# Revit family: QMXU
name_source: partatom
category: Mechanical Equipment
units: mm (PartAtom-declared; Revit-internal decimal feet)

## family parameters
Always vertical = Yes
Cut with Voids When Loaded = No
Part Type = Normal
Room Calculation Point = No
Round Connector Dimension = Use Diameter
Shared = No
Work Plane-Based = No

## types (35) — shared parameters
0 = 0' - 0"
1" = 0' - 1"
1.5 = 0' - 1 1/2"
2" = 0' - 2"
2' = 2' - 0"
3" = 0' - 3"
4" = 0' - 4"
Manufacturer = Loren Cook Company
ONE EIGTH = 0' - 0 1/8"
URL = www.lorencook.com

## per-type parameters (varying)
- 90_QMXU: (B/2)-.125"=0' - 9 7/8"; (FAN_RADIUS)*.75=0' - 4 13/16"; A=3' - 4 9/16"; A/2=1' - 8 9/32"; B=1' - 8"; B/2=0' - 10"; C=0' - 3"; C/2=0' - 1 1/2"; D=3' - 1 3/8"; D-(G/2)=2' - 5 7/8"; DC/2=0' - 6 13/32"; DUCT_COLLAR=1' - 0 13/16"; E=1' - 10 1/2"; F=1' - 9 1/4"; FAN_DIA=1' - 0 13/16"; FAN_RAD+1.5"=0' - 7 29/32"; FAN_RADIUS=0' - 6 13/32"; FAN_RADIUS/5=0' - 1 9/32"; G=1' - 3"; G/2=0' - 7 1/2"; MC_LENGTH=-1' - 3 29/32"; Model=QMXU; QMX_LENGTH=1' - 7 7/8"; T_SQ=1' - 3 1/2"; T_SQ/2=0' - 7 3/4"; Type Comments=Mixed-Flow Upblast Blower Low Pressure Belt Drive Arrangement 9
- 300_QMXU: (B/2)-.125"=2' - 2 7/8"; (FAN_RADIUS)*.75=1' - 3 15/16"; A=7' - 6 1/4"; A/2=3' - 9 1/8"; B=4' - 6"; B/2=2' - 3"; C=0' - 3"; C/2=0' - 1 1/2"; D=6' - 10"; D-(G/2)=5' - 6 3/4"; DC/2=1' - 9 1/4"; DUCT_COLLAR=3' - 6 1/2"; E=3' - 4"; F=3' - 1 5/8"; FAN_DIA=3' - 6 1/2"; FAN_RAD+1.5"=1' - 10 3/4"; FAN_RADIUS=1' - 9 1/4"; FAN_RADIUS/5=0' - 4 1/4"; G=2' - 6 1/2"; G/2=1' - 3 1/4"; MC_LENGTH=-3' - 7 3/16"; Model=QMXU; QMX_LENGTH=4' - 6"; T_SQ=4' - 1 1/2"; T_SQ/2=2' - 0 3/4"; Type Comments=Mixed-Flow Upblast Blower Low Pressure Belt Drive Arrangement 9
- 120_QMXU: (B/2)-.125"=0' - 11 7/8"; (FAN_RADIUS)*.75=0' - 6 13/32"; A=3' - 9 11/16"; A/2=1' - 10 27/32"; B=2' - 0"; B/2=1' - 0"; C=0' - 3"; C/2=0' - 1 1/2"; D=3' - 7 5/8"; D-(G/2)=2' - 11 1/8"; DC/2=0' - 8 17/32"; DUCT_COLLAR=1' - 5 1/16"; E=2' - 1 3/8"; F=2' - 0 3/8"; FAN_DIA=1' - 5 1/16"; FAN_RAD+1.5"=0' - 10 1/32"; FAN_RADIUS=0' - 8 17/32"; FAN_RADIUS/5=0' - 1 23/32"; G=1' - 5"; G/2=0' - 8 1/2"; MC_LENGTH=-1' - 7 3/16"; Model=QMXU; QMX_LENGTH=2' - 0"; T_SQ=1' - 7 1/2"; T_SQ/2=0' - 9 3/4"; Type Comments=Mixed-Flow Upblast Blower Low Pressure Belt Drive Arrangement 9
- 135_QMXU: (B/2)-.125"=1' - 0 7/8"; (FAN_RADIUS)*.75=0' - 7 7/32"; A=4' - 1 11/16"; A/2=2' - 0 27/32"; B=2' - 2"; B/2=1' - 1"; C=0' - 3"; C/2=0' - 1 1/2"; D=3' - 10 1/2"; D-(G/2)=3' - 1 1/2"; DC/2=0' - 9 5/8"; DUCT_COLLAR=1' - 7 1/4"; E=2' - 3 1/4"; F=2' - 1 3/8"; FAN_DIA=1' - 7 1/4"; FAN_RAD+1.5"=0' - 11 1/8"; FAN_RADIUS=0' - 9 5/8"; FAN_RADIUS/5=0' - 1 15/16"; G=1' - 6"; G/2=0' - 9"; MC_LENGTH=-1' - 9 19/32"; Model=QMXU; QMX_LENGTH=2' - 3"; T_SQ=1' - 9 1/2"; T_SQ/2=0' - 10 3/4"; Type Comments=Mixed-Flow Upblast Blower Low Pressure Belt Drive Arrangement 9
- 165_QMXU: (B/2)-.125"=1' - 5 3/8"; (FAN_RADIUS)*.75=0' - 8 13/16"; A=4' - 10 11/16"; A/2=2' - 5 11/32"; B=2' - 11"; B/2=1' - 5 1/2"; C=0' - 3"; C/2=0' - 1 1/2"; D=4' - 7"; D-(G/2)=3' - 8 1/2"; DC/2=0' - 11 3/4"; DUCT_COLLAR=1' - 11 1/2"; E=2' - 5 13/16"; F=2' - 3 1/8"; FAN_DIA=1' - 11 1/2"; FAN_RAD+1.5"=1' - 1 1/4"; FAN_RADIUS=0' - 11 3/4"; FAN_RADIUS/5=0' - 2 11/32"; G=1' - 9"; G/2=0' - 10 1/2"; MC_LENGTH=-2' - 2 13/32"; Model=QMXU; QMX_LENGTH=2' - 9"; T_SQ=2' - 6 1/2"; T_SQ/2=1' - 3 1/4"; Type Comments=Mixed-Flow Upblast Blower Low Pressure Belt Drive Arrangement 9
- 180_QMXU: (B/2)-.125"=1' - 6 3/8"; (FAN_RADIUS)*.75=0' - 9 5/8"; A=5' - 1 11/16"; A/2=2' - 6 27/32"; B=3' - 1"; B/2=1' - 6 1/2"; C=0' - 3"; C/2=0' - 1 1/2"; D=4' - 9 3/4"; D-(G/2)=3' - 10 3/4"; DC/2=1' - 0 13/16"; DUCT_COLLAR=2' - 1 5/8"; E=2' - 6 3/4"; F=2' - 4 1/8"; FAN_DIA=2' - 1 5/8"; FAN_RAD+1.5"=1' - 2 5/16"; FAN_RADIUS=1' - 0 13/16"; FAN_RADIUS/5=0' - 2 9/16"; G=1' - 10"; G/2=0' - 11"; MC_LENGTH=-2' - 4"; Model=QMXU; QMX_LENGTH=2' - 11"; T_SQ=2' - 8 1/2"; T_SQ/2=1' - 4 1/4"; Type Comments=Mixed-Flow Upblast Blower Low Pressure Belt Drive Arrangement 9
- 202_QMXU: (B/2)-.125"=1' - 7 7/8"; (FAN_RADIUS)*.75=0' - 9 5/8"; A=5' - 5 11/16"; A/2=2' - 8 27/32"; B=3' - 4"; B/2=1' - 8"; C=0' - 3"; C/2=0' - 1 1/2"; D=5' - 1 13/16"; D-(G/2)=4' - 2 1/16"; DC/2=1' - 2 3/8"; DUCT_COLLAR=2' - 4 3/4"; E=2' - 8 1/8"; F=2' - 5 1/2"; FAN_DIA=2' - 1 5/8"; FAN_RAD+1.5"=1' - 2 5/16"; FAN_RADIUS=1' - 0 13/16"; FAN_RADIUS/5=0' - 2 9/16"; G=1' - 11 1/2"; G/2=0' - 11 3/4"; MC_LENGTH=-2' - 4"; Model=QMXU; QMX_LENGTH=2' - 11"; T_SQ=2' - 11 1/2"; T_SQ/2=1' - 5 3/4"; Type Comments=Mixed-Flow Upblast Blower Low Pressure Belt Drive Arrangement 9
- 225_QMXU: (B/2)-.125"=1' - 9 3/8"; (FAN_RADIUS)*.75=0' - 11 31/32"; A=5' - 10 11/16"; A/2=2' - 11 11/32"; B=3' - 7"; B/2=1' - 9 1/2"; C=0' - 3"; C/2=0' - 1 1/2"; D=5' - 8 1/8"; D-(G/2)=4' - 7 5/8"; DC/2=1' - 3 31/32"; DUCT_COLLAR=2' - 7 15/16"; E=2' - 11 1/2"; F=2' - 9"; FAN_DIA=2' - 7 15/16"; FAN_RAD+1.5"=1' - 5 15/32"; FAN_RADIUS=1' - 3 31/32"; FAN_RADIUS/5=0' - 3 3/16"; G=2' - 1"; G/2=1' - 0 1/2"; MC_LENGTH=-2' - 8 13/16"; Model=QMXU; QMX_LENGTH=3' - 5"; T_SQ=3' - 2 1/2"; T_SQ/2=1' - 7 1/4"; Type Comments=Mixed-Flow Upblast Blower Low Pressure Belt Drive Arrangement 9
- 245_QMXU: (B/2)-.125"=1' - 10 7/8"; (FAN_RADIUS)*.75=1' - 1 1/32"; A=6' - 4 5/8"; A/2=3' - 2 5/16"; B=3' - 10"; B/2=1' - 11"; C=0' - 3"; C/2=0' - 1 1/2"; D=5' - 11 13/16"; D-(G/2)=4' - 10 5/16"; DC/2=1' - 5 3/8"; DUCT_COLLAR=2' - 10 3/4"; E=3' - 0 5/8"; F=2' - 10 1/8"; FAN_DIA=2' - 10 3/4"; FAN_RAD+1.5"=1' - 6 7/8"; FAN_RADIUS=1' - 5 3/8"; FAN_RADIUS/5=0' - 3 15/32"; G=2' - 3"; G/2=1' - 1 1/2"; MC_LENGTH=-2' - 11 19/32"; Model=QMXU; QMX_LENGTH=3' - 8 1/2"; T_SQ=3' - 5 1/2"; T_SQ/2=1' - 8 3/4"; Type Comments=Mixed-Flow Upblast Blower Low Pressure Belt Drive Arrangement 9
- 270_QMXU: (B/2)-.125"=2' - 0 7/8"; (FAN_RADIUS)*.75=1' - 2 3/8"; A=6' - 8 7/8"; A/2=3' - 4 7/16"; B=4' - 2"; B/2=2' - 1"; C=0' - 3"; C/2=0' - 1 1/2"; D=6' - 4 5/16"; D-(G/2)=5' - 2 1/16"; DC/2=1' - 7 5/32"; DUCT_COLLAR=3' - 2 5/16"; E=3' - 2"; F=2' - 11 9/16"; FAN_DIA=3' - 2 5/16"; FAN_RAD+1.5"=1' - 8 21/32"; FAN_RADIUS=1' - 7 5/32"; FAN_RADIUS/5=0' - 3 27/32"; G=2' - 4 1/2"; G/2=1' - 2 1/4"; MC_LENGTH=-3' - 1 19/32"; Model=QMXU; QMX_LENGTH=3' - 11"; T_SQ=3' - 9 1/2"; T_SQ/2=1' - 10 3/4"; Type Comments=Mixed-Flow Upblast Blower Low Pressure Belt Drive Arrangement 9
- 120_QMXU-HP: (B/2)-.125"=0' - 11 7/8"; (FAN_RADIUS)*.75=0' - 6 13/32"; A=3' - 9 11/16"; A/2=1' - 10 27/32"; B=2' - 0"; B/2=1' - 0"; C=0' - 3"; C/2=0' - 1 1/2"; D=3' - 7 5/8"; D-(G/2)=2' - 11 1/8"; DC/2=0' - 8 17/32"; DUCT_COLLAR=1' - 5 1/16"; E=2' - 1 3/8"; F=2' - 0 3/8"; FAN_DIA=1' - 5 1/16"; FAN_RAD+1.5"=0' - 10 1/32"; FAN_RADIUS=0' - 8 17/32"; FAN_RADIUS/5=0' - 1 23/32"; G=1' - 5"; G/2=0' - 8 1/2"; MC_LENGTH=-1' - 7 3/16"; Model=QMXU-HP; QMX_LENGTH=2' - 0"; T_SQ=1' - 7 1/2"; T_SQ/2=0' - 9 3/4"; Type Comments=Mixed-Flow Upblast Blower High Pressure Belt Drive Arrangement 9
- 135_QMXU-HP: (B/2)-.125"=1' - 0 7/8"; (FAN_RADIUS)*.75=0' - 7 7/32"; A=4' - 1 11/16"; A/2=2' - 0 27/32"; B=2' - 2"; B/2=1' - 1"; C=0' - 3"; C/2=0' - 1 1/2"; D=3' - 10 1/2"; D-(G/2)=3' - 1 1/2"; DC/2=0' - 9 5/8"; DUCT_COLLAR=1' - 7 1/4"; E=2' - 3 1/4"; F=2' - 1 3/8"; FAN_DIA=1' - 7 1/4"; FAN_RAD+1.5"=0' - 11 1/8"; FAN_RADIUS=0' - 9 5/8"; FAN_RADIUS/5=0' - 1 15/16"; G=1' - 6"; G/2=0' - 9"; MC_LENGTH=-1' - 9 19/32"; Model=QMXU-HP; QMX_LENGTH=2' - 3"; T_SQ=1' - 9 1/2"; T_SQ/2=0' - 10 3/4"; Type Comments=Mixed-Flow Upblast Blower High Pressure Belt Drive Arrangement 9
- 150_QMXU-HP: (B/2)-.125"=1' - 2 7/8"; (FAN_RADIUS)*.75=0' - 8 1/32"; A=4' - 6 11/16"; A/2=2' - 3 11/32"; B=2' - 6"; B/2=1' - 3"; C=0' - 3"; C/2=0' - 1 1/2"; D=4' - 3"; D-(G/2)=3' - 5"; DC/2=0' - 10 11/16"; DUCT_COLLAR=1' - 9 3/8"; E=2' - 4"; F=2' - 2 1/8"; FAN_DIA=1' - 9 3/8"; FAN_RAD+1.5"=1' - 0 3/16"; FAN_RADIUS=0' - 10 11/16"; FAN_RADIUS/5=0' - 2 1/8"; G=1' - 8"; G/2=0' - 10"; MC_LENGTH=-2' - 0"; Model=QMXU-HP; QMX_LENGTH=2' - 6"; T_SQ=2' - 1 1/2"; T_SQ/2=1' - 0 3/4"; Type Comments=Mixed-Flow Upblast Blower High Pressure Belt Drive Arrangement 9
- 165_QMXU-HP: (B/2)-.125"=1' - 5 3/8"; (FAN_RADIUS)*.75=0' - 8 13/16"; A=4' - 10 11/16"; A/2=2' - 5 11/32"; B=2' - 11"; B/2=1' - 5 1/2"; C=0' - 3"; C/2=0' - 1 1/2"; D=4' - 7"; D-(G/2)=3' - 8 1/2"; DC/2=0' - 11 3/4"; DUCT_COLLAR=1' - 11 1/2"; E=2' - 5 13/16"; F=2' - 3 1/8"; FAN_DIA=1' - 11 1/2"; FAN_RAD+1.5"=1' - 1 1/4"; FAN_RADIUS=0' - 11 3/4"; FAN_RADIUS/5=0' - 2 11/32"; G=1' - 9"; G/2=0' - 10 1/2"; MC_LENGTH=-2' - 2 13/32"; Model=QMXU-HP; QMX_LENGTH=2' - 9"; T_SQ=2' - 6 1/2"; T_SQ/2=1' - 3 1/4"; Type Comments=Mixed-Flow Upblast Blower High Pressure Belt Drive Arrangement 9
- 180_QMXU-HP: (B/2)-.125"=1' - 6 3/8"; (FAN_RADIUS)*.75=0' - 9 5/8"; A=5' - 1 11/16"; A/2=2' - 6 27/32"; B=3' - 1"; B/2=1' - 6 1/2"; C=0' - 3"; C/2=0' - 1 1/2"; D=4' - 9 3/4"; D-(G/2)=3' - 10 3/4"; DC/2=1' - 0 13/16"; DUCT_COLLAR=2' - 1 5/8"; E=2' - 6 3/4"; F=2' - 4 1/8"; FAN_DIA=2' - 1 5/8"; FAN_RAD+1.5"=1' - 2 5/16"; FAN_RADIUS=1' - 0 13/16"; FAN_RADIUS/5=0' - 2 9/16"; G=1' - 10"; G/2=0' - 11"; MC_LENGTH=-2' - 4"; Model=QMXU-HP; QMX_LENGTH=2' - 11"; T_SQ=2' - 8 1/2"; T_SQ/2=1' - 4 1/4"; Type Comments=Mixed-Flow Upblast Blower High Pressure Belt Drive Arrangement 9
- 202_QMXU-HP: (B/2)-.125"=1' - 7 7/8"; (FAN_RADIUS)*.75=0' - 9 5/8"; A=5' - 5 11/16"; A/2=2' - 8 27/32"; B=3' - 4"; B/2=1' - 8"; C=0' - 3"; C/2=0' - 1 1/2"; D=5' - 1 13/16"; D-(G/2)=4' - 2 1/16"; DC/2=1' - 2 3/8"; DUCT_COLLAR=2' - 4 3/4"; E=2' - 8 1/8"; F=2' - 5 1/2"; FAN_DIA=2' - 1 5/8"; FAN_RAD+1.5"=1' - 2 5/16"; FAN_RADIUS=1' - 0 13/16"; FAN_RADIUS/5=0' - 2 9/16"; G=1' - 11 1/2"; G/2=0' - 11 3/4"; MC_LENGTH=-2' - 4"; Model=QMXU-HP; QMX_LENGTH=2' - 11"; T_SQ=2' - 11 1/2"; T_SQ/2=1' - 5 3/4"; Type Comments=Mixed-Flow Upblast Blower High Pressure Belt Drive Arrangement 9
- 225_QMXU-HP: (B/2)-.125"=1' - 9 3/8"; (FAN_RADIUS)*.75=0' - 11 31/32"; A=5' - 10 11/16"; A/2=2' - 11 11/32"; B=3' - 7"; B/2=1' - 9 1/2"; C=0' - 3"; C/2=0' - 1 1/2"; D=5' - 8 1/8"; D-(G/2)=4' - 7 5/8"; DC/2=1' - 3 31/32"; DUCT_COLLAR=2' - 7 15/16"; E=2' - 11 1/2"; F=2' - 9"; FAN_DIA=2' - 7 15/16"; FAN_RAD+1.5"=1' - 5 15/32"; FAN_RADIUS=1' - 3 31/32"; FAN_RADIUS/5=0' - 3 3/16"; G=2' - 1"; G/2=1' - 0 1/2"; MC_LENGTH=-2' - 8 13/16"; Model=QMXU-HP; QMX_LENGTH=3' - 5"; T_SQ=3' - 2 1/2"; T_SQ/2=1' - 7 1/4"; Type Comments=Mixed-Flow Upblast Blower High Pressure Belt Drive Arrangement 9
- 245_QMXU-HP: (B/2)-.125"=1' - 10 7/8"; (FAN_RADIUS)*.75=1' - 1 1/32"; A=6' - 4 5/8"; A/2=3' - 2 5/16"; B=3' - 10"; B/2=1' - 11"; C=0' - 3"; C/2=0' - 1 1/2"; D=5' - 11 13/16"; D-(G/2)=4' - 10 5/16"; DC/2=1' - 5 3/8"; DUCT_COLLAR=2' - 10 3/4"; E=3' - 0 5/8"; F=2' - 10 1/8"; FAN_DIA=2' - 10 3/4"; FAN_RAD+1.5"=1' - 6 7/8"; FAN_RADIUS=1' - 5 3/8"; FAN_RADIUS/5=0' - 3 15/32"; G=2' - 3"; G/2=1' - 1 1/2"; MC_LENGTH=-2' - 11 19/32"; Model=QMXU-HP; QMX_LENGTH=3' - 8 1/2"; T_SQ=3' - 5 1/2"; T_SQ/2=1' - 8 3/4"; Type Comments=Mixed-Flow Upblast Blower High Pressure Belt Drive Arrangement 9
- 270_QMXU-HP: (B/2)-.125"=2' - 0 7/8"; (FAN_RADIUS)*.75=1' - 2 3/8"; A=6' - 8 7/8"; A/2=3' - 4 7/16"; B=4' - 2"; B/2=2' - 1"; C=0' - 3"; C/2=0' - 1 1/2"; D=6' - 4 5/16"; D-(G/2)=5' - 2 1/16"; DC/2=1' - 7 5/32"; DUCT_COLLAR=3' - 2 5/16"; E=3' - 2"; F=2' - 11 9/16"; FAN_DIA=3' - 2 5/16"; FAN_RAD+1.5"=1' - 8 21/32"; FAN_RADIUS=1' - 7 5/32"; FAN_RADIUS/5=0' - 3 27/32"; G=2' - 4 1/2"; G/2=1' - 2 1/4"; MC_LENGTH=-3' - 1 19/32"; Model=QMXU-HP; QMX_LENGTH=3' - 11"; T_SQ=3' - 9 1/2"; T_SQ/2=1' - 10 3/4"; Type Comments=Mixed-Flow Upblast Blower High Pressure Belt Drive Arrangement 9
- 300_QMXU-HP: (B/2)-.125"=2' - 2 7/8"; (FAN_RADIUS)*.75=1' - 3 15/16"; A=7' - 6 1/4"; A/2=3' - 9 1/8"; B=4' - 6"; B/2=2' - 3"; C=0' - 3"; C/2=0' - 1 1/2"; D=6' - 10"; D-(G/2)=5' - 6 3/4"; DC/2=1' - 9 1/4"; DUCT_COLLAR=3' - 6 1/2"; E=3' - 4"; F=3' - 1 5/8"; FAN_DIA=3' - 6 1/2"; FAN_RAD+1.5"=1' - 10 3/4"; FAN_RADIUS=1' - 9 1/4"; FAN_RADIUS/5=0' - 4 1/4"; G=2' - 6 1/2"; G/2=1' - 3 1/4"; MC_LENGTH=-3' - 7 3/16"; Model=QMXU-HP; QMX_LENGTH=4' - 6"; T_SQ=4' - 1 1/2"; T_SQ/2=2' - 0 3/4"; Type Comments=Mixed-Flow Upblast Blower High Pressure Belt Drive Arrangement 9
- 90_QMXU-HP: (B/2)-.125"=0' - 9 7/8"; (FAN_RADIUS)*.75=0' - 4 13/16"; A=3' - 4 9/16"; A/2=1' - 8 9/32"; B=1' - 8"; B/2=0' - 10"; C=0' - 3"; C/2=0' - 1 1/2"; D=3' - 1 3/8"; D-(G/2)=2' - 5 7/8"; DC/2=0' - 6 13/32"; DUCT_COLLAR=1' - 0 13/16"; E=1' - 10 1/2"; F=1' - 9 1/4"; FAN_DIA=1' - 0 13/16"; FAN_RAD+1.5"=0' - 7 29/32"; FAN_RADIUS=0' - 6 13/32"; FAN_RADIUS/5=0' - 1 9/32"; G=1' - 3"; G/2=0' - 7 1/2"; MC_LENGTH=-1' - 3 29/32"; Model=QMXU-HP; QMX_LENGTH=1' - 7 7/8"; T_SQ=1' - 3 1/2"; T_SQ/2=0' - 7 3/4"; Type Comments=Mixed-Flow Upblast Blower High Pressure Belt Drive Arrangement 9
- 330_QMXU: (B/2)-.125"=2' - 4 7/8"; (FAN_RADIUS)*.75=1' - 5 17/32"; A=7' - 2 3/4"; A/2=3' - 7 3/8"; B=4' - 10"; B/2=2' - 5"; C=0' - 3"; C/2=0' - 1 1/2"; D=7' - 5 1/4"; D-(G/2)=6' - 1"; DC/2=1' - 11 3/8"; DUCT_COLLAR=3' - 10 3/4"; E=3' - 8 5/8"; F=3' - 5 11/16"; FAN_DIA=3' - 10 3/4"; FAN_RAD+1.5"=2' - 0 7/8"; FAN_RADIUS=1' - 11 3/8"; FAN_RADIUS/5=0' - 4 11/16"; G=2' - 8 1/2"; G/2=1' - 4 1/4"; MC_LENGTH=-3' - 1 13/32"; Model=QMXU; QMX_LENGTH=3' - 10 3/4"; T_SQ=4' - 5 1/2"; T_SQ/2=2' - 2 3/4"; Type Comments=Mixed-Flow Upblast Blower Low Pressure Belt Drive Arrangement 9
- 365_QMXU: (B/2)-.125"=2' - 7 7/8"; (FAN_RADIUS)*.75=1' - 7 13/32"; A=8' - 8 7/8"; A/2=4' - 4 7/16"; B=5' - 4"; B/2=2' - 8"; C=0' - 3"; C/2=0' - 1 1/2"; D=8' - 0 1/4"; D-(G/2)=6' - 6 3/4"; DC/2=2' - 1 7/8"; DUCT_COLLAR=4' - 3 3/4"; E=3' - 10 5/8"; F=3' - 7 5/8"; FAN_DIA=4' - 3 3/4"; FAN_RAD+1.5"=2' - 3 3/8"; FAN_RADIUS=2' - 1 7/8"; FAN_RADIUS/5=0' - 5 3/16"; G=2' - 11"; G/2=1' - 5 1/2"; MC_LENGTH=-4' - 3 3/16"; Model=QMXU; QMX_LENGTH=5' - 4"; T_SQ=4' - 11 1/2"; T_SQ/2=2' - 5 3/4"; Type Comments=Mixed-Flow Upblast Blower Low Pressure Belt Drive Arrangement 9
- 402_QMXU: (B/2)-.125"=2' - 10 3/8"; (FAN_RADIUS)*.75=1' - 9 11/32"; A=9' - 4 3/8"; A/2=4' - 8 3/16"; B=5' - 9"; B/2=2' - 10 1/2"; C=0' - 3"; C/2=0' - 1 1/2"; D=8' - 9"; D-(G/2)=7' - 2"; DC/2=2' - 4 15/32"; DUCT_COLLAR=4' - 8 15/16"; E=4' - 4"; F=4' - 0 3/8"; FAN_DIA=4' - 8 15/16"; FAN_RAD+1.5"=2' - 5 31/32"; FAN_RADIUS=2' - 4 15/32"; FAN_RADIUS/5=0' - 5 11/16"; G=3' - 2"; G/2=1' - 7"; MC_LENGTH=-4' - 6 13/16"; Model=QMXU; QMX_LENGTH=5' - 8 1/2"; T_SQ=5' - 4 1/2"; T_SQ/2=2' - 8 1/4"; Type Comments=Mixed-Flow Upblast Blower Low Pressure Belt Drive Arrangement 9
- 445_QMXU: (B/2)-.125"=3' - 1 3/8"; (FAN_RADIUS)*.75=1' - 11 21/32"; A=10' - 0 7/8"; A/2=5' - 0 7/16"; B=6' - 3"; B/2=3' - 1 1/2"; C=0' - 3"; C/2=0' - 1 1/2"; D=9' - 4 7/16"; D-(G/2)=7' - 7 15/16"; DC/2=2' - 7 17/32"; DUCT_COLLAR=5' - 3 1/16"; E=4' - 6 3/8"; F=4' - 2 11/16"; FAN_DIA=5' - 3 1/16"; FAN_RAD+1.5"=2' - 9 1/32"; FAN_RADIUS=2' - 7 17/32"; FAN_RADIUS/5=0' - 6 5/16"; G=3' - 5"; G/2=1' - 8 1/2"; MC_LENGTH=-4' - 11 3/16"; Model=QMXU; QMX_LENGTH=6' - 2"; T_SQ=5' - 10 1/2"; T_SQ/2=2' - 11 1/4"; Type Comments=Mixed-Flow Upblast Blower Low Pressure Belt Drive Arrangement 9
- 490_QMXU: (B/2)-.125"=3' - 4 7/8"; (FAN_RADIUS)*.75=2' - 2 1/32"; A=10' - 11 3/8"; A/2=5' - 5 11/16"; B=6' - 10"; B/2=3' - 5"; C=0' - 4"; C/2=0' - 2"; D=10' - 2 1/2"; D-(G/2)=8' - 4 1/2"; DC/2=2' - 10 11/16"; DUCT_COLLAR=5' - 9 3/8"; E=4' - 11 5/8"; F=4' - 7 1/16"; FAN_DIA=5' - 9 3/8"; FAN_RAD+1.5"=3' - 0 3/16"; FAN_RADIUS=2' - 10 11/16"; FAN_RADIUS/5=0' - 6 15/16"; G=3' - 8"; G/2=1' - 10"; MC_LENGTH=-5' - 4 13/32"; Model=QMXU; QMX_LENGTH=6' - 8 1/2"; T_SQ=6' - 5 1/2"; T_SQ/2=3' - 2 3/4"; Type Comments=Mixed-Flow Upblast Blower Low Pressure Belt Drive Arrangement 9
- 540_QMXU: (B/2)-.125"=3' - 8 7/8"; (FAN_RADIUS)*.75=2' - 4 21/32"; A=11' - 9 7/8"; A/2=5' - 10 15/16"; B=7' - 6"; B/2=3' - 9"; C=0' - 4"; C/2=0' - 2"; D=10' - 11 7/8"; D-(G/2)=8' - 11 7/8"; DC/2=3' - 2 7/32"; DUCT_COLLAR=6' - 4 7/16"; E=5' - 2 1/4"; F=4' - 9 3/4"; FAN_DIA=6' - 4 7/16"; FAN_RAD+1.5"=3' - 3 23/32"; FAN_RADIUS=3' - 2 7/32"; FAN_RADIUS/5=0' - 7 21/32"; G=4' - 0"; G/2=2' - 0"; MC_LENGTH=-5' - 9 19/32"; Model=QMXU; QMX_LENGTH=7' - 3"; T_SQ=7' - 1 1/2"; T_SQ/2=3' - 6 3/4"; Type Comments=Mixed-Flow Upblast Blower Low Pressure Belt Drive Arrangement 9
- 600_QMXU: (B/2)-.125"=4' - 0 7/8"; (FAN_RADIUS)*.75=2' - 7 27/32"; A=12' - 10 3/8"; A/2=6' - 5 3/16"; B=8' - 2"; B/2=4' - 1"; C=0' - 4"; C/2=0' - 2"; D=11' - 10"; D-(G/2)=9' - 8"; DC/2=3' - 6 7/16"; DUCT_COLLAR=7' - 0 7/8"; E=5' - 5 1/2"; F=5' - 1"; FAN_DIA=7' - 0 7/8"; FAN_RAD+1.5"=3' - 7 15/16"; FAN_RADIUS=3' - 6 7/16"; FAN_RADIUS/5=0' - 8 1/2"; G=4' - 4"; G/2=2' - 2"; MC_LENGTH=-6' - 4 13/32"; Model=QMXU; QMX_LENGTH=7' - 11 1/2"; T_SQ=7' - 9 1/2"; T_SQ/2=3' - 10 3/4"; Type Comments=Mixed-Flow Upblast Blower  Low Pressure Belt Drive Arrangement 9
- 330_QMXU-HP: (B/2)-.125"=2' - 4 7/8"; (FAN_RADIUS)*.75=1' - 5 17/32"; A=7' - 2 3/4"; A/2=3' - 7 3/8"; B=4' - 10"; B/2=2' - 5"; C=0' - 3"; C/2=0' - 1 1/2"; D=7' - 5 1/4"; D-(G/2)=6' - 1"; DC/2=1' - 11 3/8"; DUCT_COLLAR=3' - 10 3/4"; E=3' - 8 5/8"; F=3' - 5 11/16"; FAN_DIA=3' - 10 3/4"; FAN_RAD+1.5"=2' - 0 7/8"; FAN_RADIUS=1' - 11 3/8"; FAN_RADIUS/5=0' - 4 11/16"; G=2' - 8 1/2"; G/2=1' - 4 1/4"; MC_LENGTH=-3' - 1 13/32"; Model=QMXU-HP; QMX_LENGTH=3' - 10 3/4"; T_SQ=4' - 5 1/2"; T_SQ/2=2' - 2 3/4"; Type Comments=Mixed-Flow Upblast Blower High Pressure Belt Drive Arrangement 9
- 365_QMXU-HP: (B/2)-.125"=2' - 7 7/8"; (FAN_RADIUS)*.75=1' - 7 13/32"; A=8' - 8 7/8"; A/2=4' - 4 7/16"; B=5' - 4"; B/2=2' - 8"; C=0' - 3"; C/2=0' - 1 1/2"; D=8' - 0 1/4"; D-(G/2)=6' - 6 3/4"; DC/2=2' - 1 7/8"; DUCT_COLLAR=4' - 3 3/4"; E=3' - 10 5/8"; F=3' - 7 5/8"; FAN_DIA=4' - 3 3/4"; FAN_RAD+1.5"=2' - 3 3/8"; FAN_RADIUS=2' - 1 7/8"; FAN_RADIUS/5=0' - 5 3/16"; G=2' - 11"; G/2=1' - 5 1/2"; MC_LENGTH=-4' - 3 3/16"; Model=QMXU-HP; QMX_LENGTH=5' - 4"; T_SQ=4' - 11 1/2"; T_SQ/2=2' - 5 3/4"; Type Comments=Mixed-Flow Upblast Blower High Pressure Belt Drive Arrangement 9
- 402_QMXU-HP: (B/2)-.125"=2' - 10 3/8"; (FAN_RADIUS)*.75=1' - 9 11/32"; A=9' - 4 3/8"; A/2=4' - 8 3/16"; B=5' - 9"; B/2=2' - 10 1/2"; C=0' - 3"; C/2=0' - 1 1/2"; D=8' - 9"; D-(G/2)=7' - 2"; DC/2=2' - 4 15/32"; DUCT_COLLAR=4' - 8 15/16"; E=4' - 4"; F=4' - 0 3/8"; FAN_DIA=4' - 8 15/16"; FAN_RAD+1.5"=2' - 5 31/32"; FAN_RADIUS=2' - 4 15/32"; FAN_RADIUS/5=0' - 5 11/16"; G=3' - 2"; G/2=1' - 7"; MC_LENGTH=-4' - 6 13/16"; Model=QMXU-HP; QMX_LENGTH=5' - 8 1/2"; T_SQ=5' - 4 1/2"; T_SQ/2=2' - 8 1/4"; Type Comments=Mixed-Flow Upblast Blower High Pressure Belt Drive Arrangement 9
- 445_QMXU-HP: (B/2)-.125"=3' - 1 3/8"; (FAN_RADIUS)*.75=1' - 11 21/32"; A=10' - 0 7/8"; A/2=5' - 0 7/16"; B=6' - 3"; B/2=3' - 1 1/2"; C=0' - 3"; C/2=0' - 1 1/2"; D=9' - 4 7/16"; D-(G/2)=7' - 7 15/16"; DC/2=2' - 7 17/32"; DUCT_COLLAR=5' - 3 1/16"; E=4' - 6 3/8"; F=4' - 2 11/16"; FAN_DIA=5' - 3 1/16"; FAN_RAD+1.5"=2' - 9 1/32"; FAN_RADIUS=2' - 7 17/32"; FAN_RADIUS/5=0' - 6 5/16"; G=3' - 5"; G/2=1' - 8 1/2"; MC_LENGTH=-4' - 11 3/16"; Model=QMXU-HP; QMX_LENGTH=6' - 2"; T_SQ=5' - 10 1/2"; T_SQ/2=2' - 11 1/4"; Type Comments=Mixed-Flow Upblast Blower High Pressure Belt Drive Arrangement 9
- 490_QMXU-HP: (B/2)-.125"=3' - 4 7/8"; (FAN_RADIUS)*.75=2' - 2 1/32"; A=10' - 11 3/8"; A/2=5' - 5 11/16"; B=6' - 10"; B/2=3' - 5"; C=0' - 4"; C/2=0' - 2"; D=10' - 2 1/2"; D-(G/2)=8' - 4 1/2"; DC/2=2' - 10 11/16"; DUCT_COLLAR=5' - 9 3/8"; E=4' - 11 5/8"; F=4' - 7 1/16"; FAN_DIA=5' - 9 3/8"; FAN_RAD+1.5"=3' - 0 3/16"; FAN_RADIUS=2' - 10 11/16"; FAN_RADIUS/5=0' - 6 15/16"; G=3' - 8"; G/2=1' - 10"; MC_LENGTH=-5' - 4 13/32"; Model=QMXU-HP; QMX_LENGTH=6' - 8 1/2"; T_SQ=6' - 5 1/2"; T_SQ/2=3' - 2 3/4"; Type Comments=Mixed-Flow Upblast Blower High Pressure Belt Drive Arrangement 9
- 540_QMXU-HP: (B/2)-.125"=3' - 8 7/8"; (FAN_RADIUS)*.75=2' - 4 21/32"; A=11' - 9 7/8"; A/2=5' - 10 15/16"; B=7' - 6"; B/2=3' - 9"; C=0' - 4"; C/2=0' - 2"; D=10' - 11 7/8"; D-(G/2)=8' - 11 7/8"; DC/2=3' - 2 7/32"; DUCT_COLLAR=6' - 4 7/16"; E=5' - 2 1/4"; F=4' - 9 3/4"; FAN_DIA=6' - 4 7/16"; FAN_RAD+1.5"=3' - 3 23/32"; FAN_RADIUS=3' - 2 7/32"; FAN_RADIUS/5=0' - 7 21/32"; G=4' - 0"; G/2=2' - 0"; MC_LENGTH=-5' - 9 19/32"; Model=QMXU-HP; QMX_LENGTH=7' - 3"; T_SQ=7' - 1 1/2"; T_SQ/2=3' - 6 3/4"; Type Comments=Mixed-Flow Upblast Blower High Pressure Belt Drive Arrangement 9
- 150_QMXU: (B/2)-.125"=1' - 2 7/8"; (FAN_RADIUS)*.75=0' - 8 1/32"; A=4' - 6 11/16"; A/2=2' - 3 11/32"; B=2' - 6"; B/2=1' - 3"; C=0' - 3"; C/2=0' - 1 1/2"; D=4' - 3"; D-(G/2)=3' - 5"; DC/2=0' - 10 11/16"; DUCT_COLLAR=1' - 9 3/8"; E=2' - 4"; F=2' - 2 1/8"; FAN_DIA=1' - 9 3/8"; FAN_RAD+1.5"=1' - 0 3/16"; FAN_RADIUS=0' - 10 11/16"; FAN_RADIUS/5=0' - 2 1/8"; G=1' - 8"; G/2=0' - 10"; MC_LENGTH=-2' - 0"; Model=QMXU; QMX_LENGTH=2' - 6"; T_SQ=2' - 1 1/2"; T_SQ/2=1' - 0 3/4"; Type Comments=Mixed-Flow Upblast Blower Low Pressure Belt Drive Arrangement 9

## geometry (parser evidence)
native form markers: Sweep x1
no freeform markers — native parametric forms only
